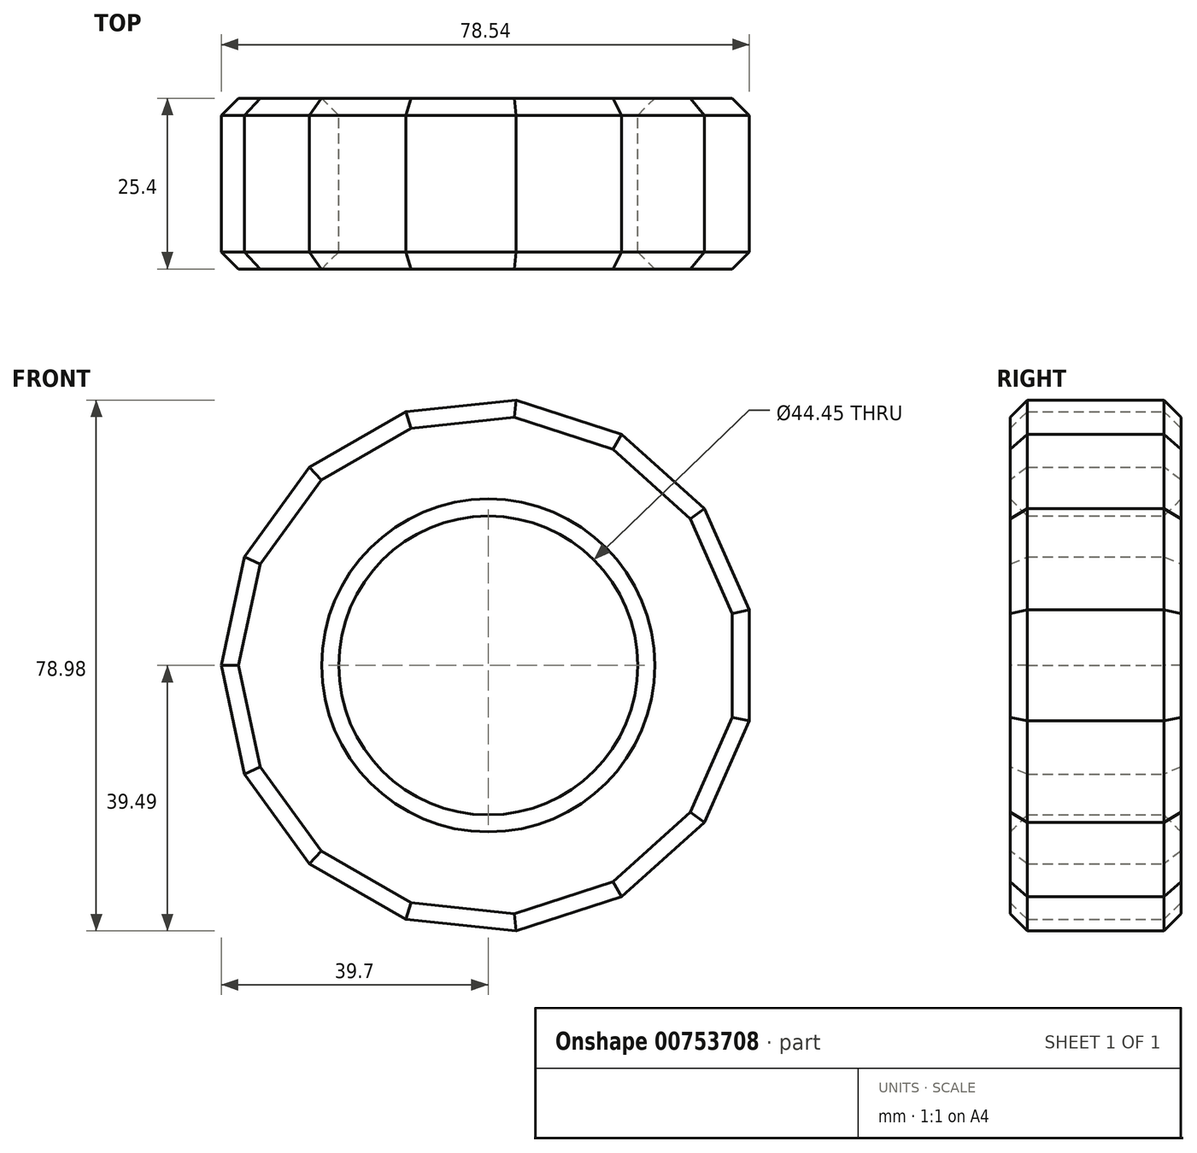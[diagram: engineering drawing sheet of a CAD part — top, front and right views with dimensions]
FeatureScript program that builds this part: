
annotation { "Feature Type Name" : "Feature", "Feature Type Description" : "" }
export const myFeature = defineFeature(function(context is Context, id is Id, definition is map)
    precondition{}
    {
        {
            var Q0;
            Q0=qCreatedBy(makeId("Front.planeOp"),FACE);
            var sketch = newSketch(context, id + "F0", { "sketchPlane" : qUnion([Q0])});
            skCircle(sketch, "E0.cCircle", {"center": v(0, 0) * mm, "radius": 39.7 * mm, "construction": true});
            skLineSegment(sketch, "E0.0", {"start": v(-39.7, 0) * mm, "end": v(-36.27, 16.15) * mm});
            skLineSegment(sketch, "E0.1", {"start": v(-36.27, 16.15) * mm, "end": v(-26.57, 29.5) * mm});
            skLineSegment(sketch, "E0.2", {"start": v(-26.57, 29.5) * mm, "end": v(-12.27, 37.76) * mm});
            skLineSegment(sketch, "E0.3", {"start": v(-12.27, 37.76) * mm, "end": v(4.15, 39.49) * mm});
            skLineSegment(sketch, "E0.4", {"start": v(4.15, 39.49) * mm, "end": v(19.85, 34.38) * mm});
            skLineSegment(sketch, "E0.5", {"start": v(19.85, 34.38) * mm, "end": v(32.12, 23.34) * mm});
            skLineSegment(sketch, "E0.6", {"start": v(32.12, 23.34) * mm, "end": v(38.84, 8.26) * mm});
            skLineSegment(sketch, "E0.7", {"start": v(38.84, 8.26) * mm, "end": v(38.84, -8.26) * mm});
            skLineSegment(sketch, "E0.8", {"start": v(38.84, -8.26) * mm, "end": v(32.12, -23.34) * mm});
            skLineSegment(sketch, "E0.9", {"start": v(32.12, -23.34) * mm, "end": v(19.85, -34.38) * mm});
            skLineSegment(sketch, "E0.10", {"start": v(19.85, -34.38) * mm, "end": v(4.15, -39.49) * mm});
            skLineSegment(sketch, "E0.11", {"start": v(4.15, -39.49) * mm, "end": v(-12.27, -37.76) * mm});
            skLineSegment(sketch, "E0.12", {"start": v(-12.27, -37.76) * mm, "end": v(-26.57, -29.5) * mm});
            skLineSegment(sketch, "E0.13", {"start": v(-26.57, -29.5) * mm, "end": v(-36.27, -16.15) * mm});
            skLineSegment(sketch, "E0.14", {"start": v(-36.27, -16.15) * mm, "end": v(-39.7, 0) * mm});
            skCircle(sketch, "E1", {"center": v(0, 0) * mm, "radius": 22.23 * mm});
            skSolve(sketch);
        }
        {
            var Q0;
            Q0=makeQuery(id+"F0.imprint","IMPRINT",FACE,{"disambiguationData":[TD([[makeQuery(id+"F0.imprint","IMPRINT",EDGE,{"derivedFrom":sQuery(id+"F0.wireOp",EDGE,"E0.0")}),-1.0]])]});
            extrude(context, id + "F1", {"entities" : qUnion([Q0]), "depth" : 25.4 * mm, "offsetDistance" : 25.4 * mm});
        }
        {
            var Q0;
            Q0=makeQuery(id+"F1.opExtrude","CAP_FACE",FACE,{"disambiguationData":[OSD([sQuery(id+"F0.wireOp",EDGE,"E0.0"),sQuery(id+"F0.wireOp",EDGE,"E0.1"),sQuery(id+"F0.wireOp",EDGE,"E0.2"),sQuery(id+"F0.wireOp",EDGE,"E0.3"),sQuery(id+"F0.wireOp",EDGE,"E0.4"),sQuery(id+"F0.wireOp",EDGE,"E0.5"),sQuery(id+"F0.wireOp",EDGE,"E0.6"),sQuery(id+"F0.wireOp",EDGE,"E0.7"),sQuery(id+"F0.wireOp",EDGE,"E0.8"),sQuery(id+"F0.wireOp",EDGE,"E0.9"),sQuery(id+"F0.wireOp",EDGE,"E0.10"),sQuery(id+"F0.wireOp",EDGE,"E0.11"),sQuery(id+"F0.wireOp",EDGE,"E0.12"),sQuery(id+"F0.wireOp",EDGE,"E0.13"),sQuery(id+"F0.wireOp",EDGE,"E0.14"),sQuery(id+"F0.wireOp",EDGE,"E1")])],"isStart":false});
            var Q1;
            Q1=makeQuery(id+"F1.opExtrude","CAP_FACE",FACE,{"disambiguationData":[OSD([sQuery(id+"F0.wireOp",EDGE,"E0.0"),sQuery(id+"F0.wireOp",EDGE,"E0.1"),sQuery(id+"F0.wireOp",EDGE,"E0.2"),sQuery(id+"F0.wireOp",EDGE,"E0.3"),sQuery(id+"F0.wireOp",EDGE,"E0.4"),sQuery(id+"F0.wireOp",EDGE,"E0.5"),sQuery(id+"F0.wireOp",EDGE,"E0.6"),sQuery(id+"F0.wireOp",EDGE,"E0.7"),sQuery(id+"F0.wireOp",EDGE,"E0.8"),sQuery(id+"F0.wireOp",EDGE,"E0.9"),sQuery(id+"F0.wireOp",EDGE,"E0.10"),sQuery(id+"F0.wireOp",EDGE,"E0.11"),sQuery(id+"F0.wireOp",EDGE,"E0.12"),sQuery(id+"F0.wireOp",EDGE,"E0.13"),sQuery(id+"F0.wireOp",EDGE,"E0.14"),sQuery(id+"F0.wireOp",EDGE,"E1")])],"isStart":true});
            chamfer(context, id + "F2", {"entities" : qUnion([Q0, Q1]), "width" : 2.54 * mm, "tangentPropagation" : true});
        }
    });
